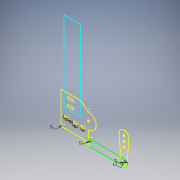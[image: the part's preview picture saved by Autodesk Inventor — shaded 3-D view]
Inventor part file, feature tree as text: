
AUTODESK INVENTOR PART (.ipt)
format: ipt  version: 2018 (Build 220112000, 112)  size: 113,664 bytes
history: native  units: mm
features: sketch x1
ambient origin geometry x8: Origin, YZ Plane, XZ Plane, XY Plane, X Axis, Y Axis, Z Axis, Center Point
feature tree (1):
  sketch  "Boceto1"  dims[d26=30.0mm d125=16.0mm d126=3.0mm d135=11.0mm d136=11.0mm d165=8.0mm d166=6.0mm d167=8.0mm d169=6.0mm d170=5.0mm]
